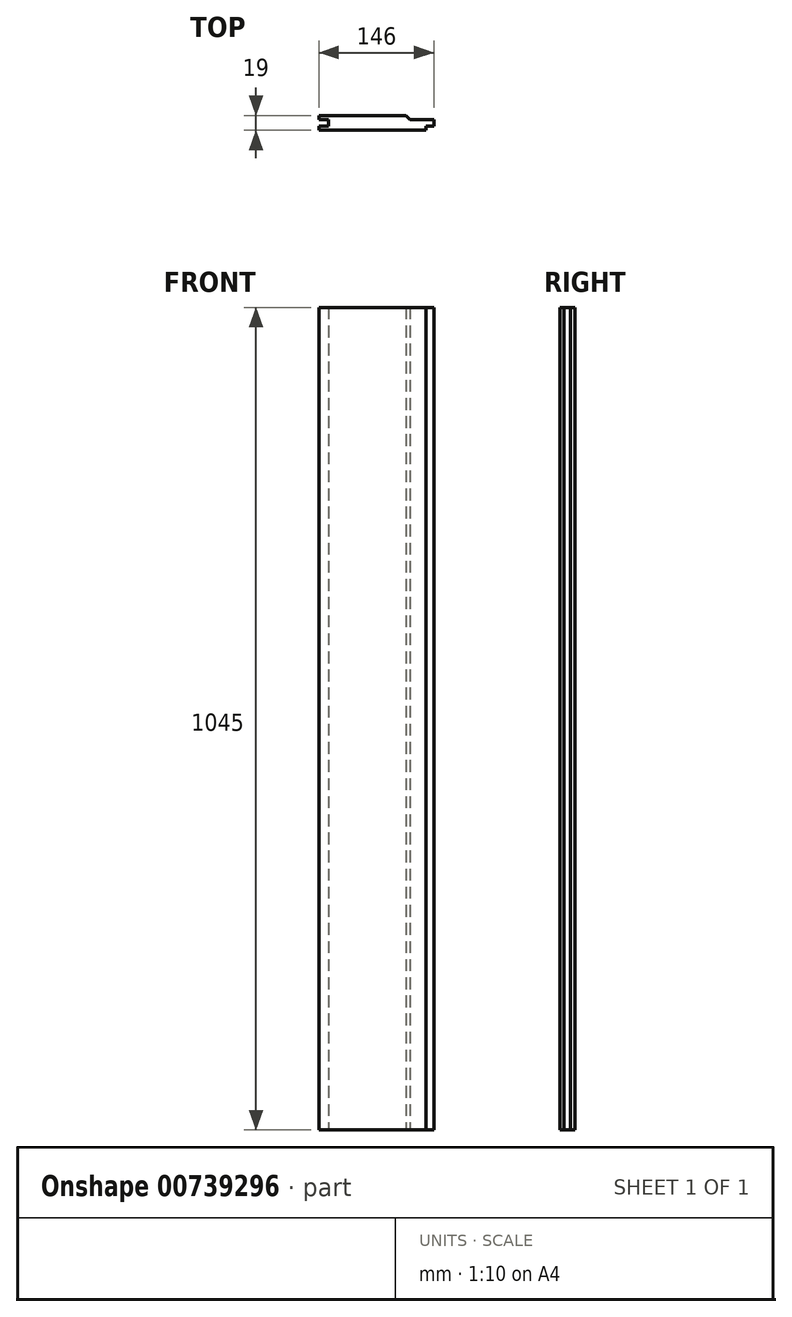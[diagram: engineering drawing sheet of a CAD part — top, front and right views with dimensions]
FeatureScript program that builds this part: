
annotation { "Feature Type Name" : "Feature", "Feature Type Description" : "" }
export const myFeature = defineFeature(function(context is Context, id is Id, definition is map)
    precondition{}
    {
        {
            var Q0;
            Q0=qCreatedBy(makeId("Top.planeOp"),FACE);
            var sketch = newSketch(context, id + "F0", { "sketchPlane" : qUnion([Q0])});
            skLineSegment(sketch, "E0.bottom", {"start": v(0, -9.5) * mm, "end": v(136, -9.5) * mm});
            skLineSegment(sketch, "E0.top", {"start": v(0, 9.5) * mm, "end": v(110.5, 9.5) * mm});
            skLineSegment(sketch, "E0.left", {"start": v(0, -9.5) * mm, "end": v(0, -4) * mm});
            skLineSegment(sketch, "E0.right", {"start": v(136, -9.5) * mm, "end": v(136, -4) * mm});
            skLineSegment(sketch, "E1", {"start": v(0, -4) * mm, "end": v(12, -4) * mm});
            skLineSegment(sketch, "E2", {"start": v(12, -4) * mm, "end": v(12, 4) * mm});
            skLineSegment(sketch, "E3", {"start": v(12, 4) * mm, "end": v(0, 4) * mm});
            skLineSegment(sketch, "E4.trimOffspring", {"start": v(0, 4) * mm, "end": v(0, 9.5) * mm});
            skLineSegment(sketch, "E5", {"start": v(136, -4) * mm, "end": v(146, -4) * mm});
            skLineSegment(sketch, "E6", {"start": v(146, -4) * mm, "end": v(146, 4) * mm});
            skLineSegment(sketch, "E7", {"start": v(146, 4) * mm, "end": v(116, 4) * mm});
            skLineSegment(sketch, "E8.trimOffspring", {"start": v(116, 4) * mm, "end": v(110.5, 9.5) * mm});
            skSolve(sketch);
        }
        {
            var Q0;
            Q0=makeQuery(id+"F0.imprint","IMPRINT",FACE,{"disambiguationData":[TD([[makeQuery(id+"F0.imprint","IMPRINT",EDGE,{"derivedFrom":sQuery(id+"F0.wireOp",EDGE,"E0.bottom")}),1.0]])]});
            extrude(context, id + "F1", {"entities" : qUnion([Q0]), "depth" : 1045 * mm, "offsetDistance" : 25 * mm});
        }
    });
